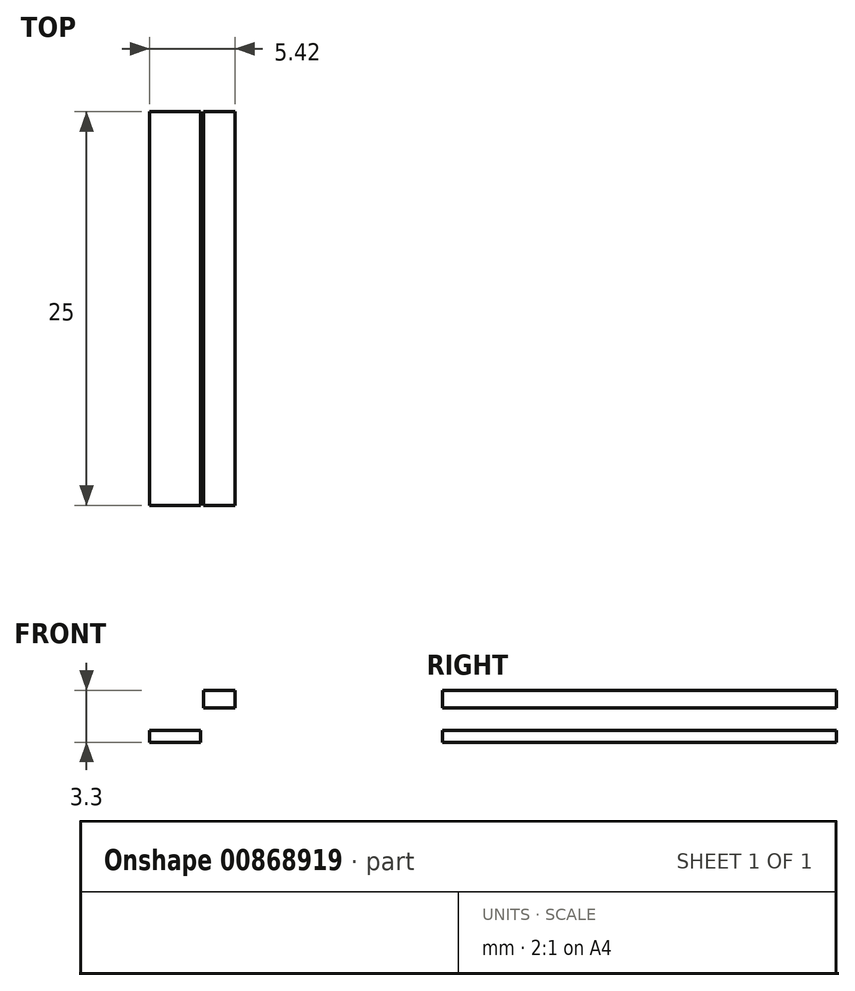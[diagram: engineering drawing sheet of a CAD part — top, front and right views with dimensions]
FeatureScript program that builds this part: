
annotation { "Feature Type Name" : "Feature", "Feature Type Description" : "" }
export const myFeature = defineFeature(function(context is Context, id is Id, definition is map)
    precondition{}
    {
        {
            var Q0;
            Q0=qCreatedBy(makeId("Front.planeOp"),FACE);
            var sketch = newSketch(context, id + "F0", { "sketchPlane" : qUnion([Q0])});
            skLineSegment(sketch, "E0.bottom", {"start": v(-1.63, -0.38) * mm, "end": v(1.63, -0.38) * mm});
            skLineSegment(sketch, "E0.top", {"start": v(-1.63, 0.38) * mm, "end": v(1.62, 0.38) * mm});
            skLineSegment(sketch, "E0.left", {"start": v(-1.62, -0.38) * mm, "end": v(-1.63, 0.37) * mm});
            skLineSegment(sketch, "E0.right", {"start": v(1.63, -0.38) * mm, "end": v(1.62, 0.38) * mm});
            skPoint(sketch, "E0.middle", {"position": v(0, 0) * mm});
            skLineSegment(sketch, "E1.bottom", {"start": v(1.8, 1.8) * mm, "end": v(3.8, 1.8) * mm});
            skLineSegment(sketch, "E1.top", {"start": v(1.8, 2.92) * mm, "end": v(3.8, 2.92) * mm});
            skLineSegment(sketch, "E1.left", {"start": v(1.8, 1.8) * mm, "end": v(1.8, 2.92) * mm});
            skLineSegment(sketch, "E1.right", {"start": v(3.8, 1.8) * mm, "end": v(3.8, 2.92) * mm});
            skPoint(sketch, "E1.middle", {"position": v(2.8, 2.36) * mm});
            skLineSegment(sketch, "E2", {"start": v(1.62, 0.38) * mm, "end": v(1.62, 1.06) * mm});
            skArc(sketch, "E3", {"start": v(1.62, 1.06) * mm, "mid": v(1.8, 1.5) * mm, "end": v(2.25, 1.69) * mm});
            skLineSegment(sketch, "E4", {"start": v(2.25, 1.69) * mm, "end": v(8.15, 1.69) * mm});
            skSolve(sketch);
        }
        {
            var Q0;
            Q0 = qSketchRegion(id + "F0", true);
            extrude(context, id + "F1", {"entities" : qUnion([Q0]), "depth" : 25 * mm, "offsetDistance" : 25 * mm});
        }
    });
